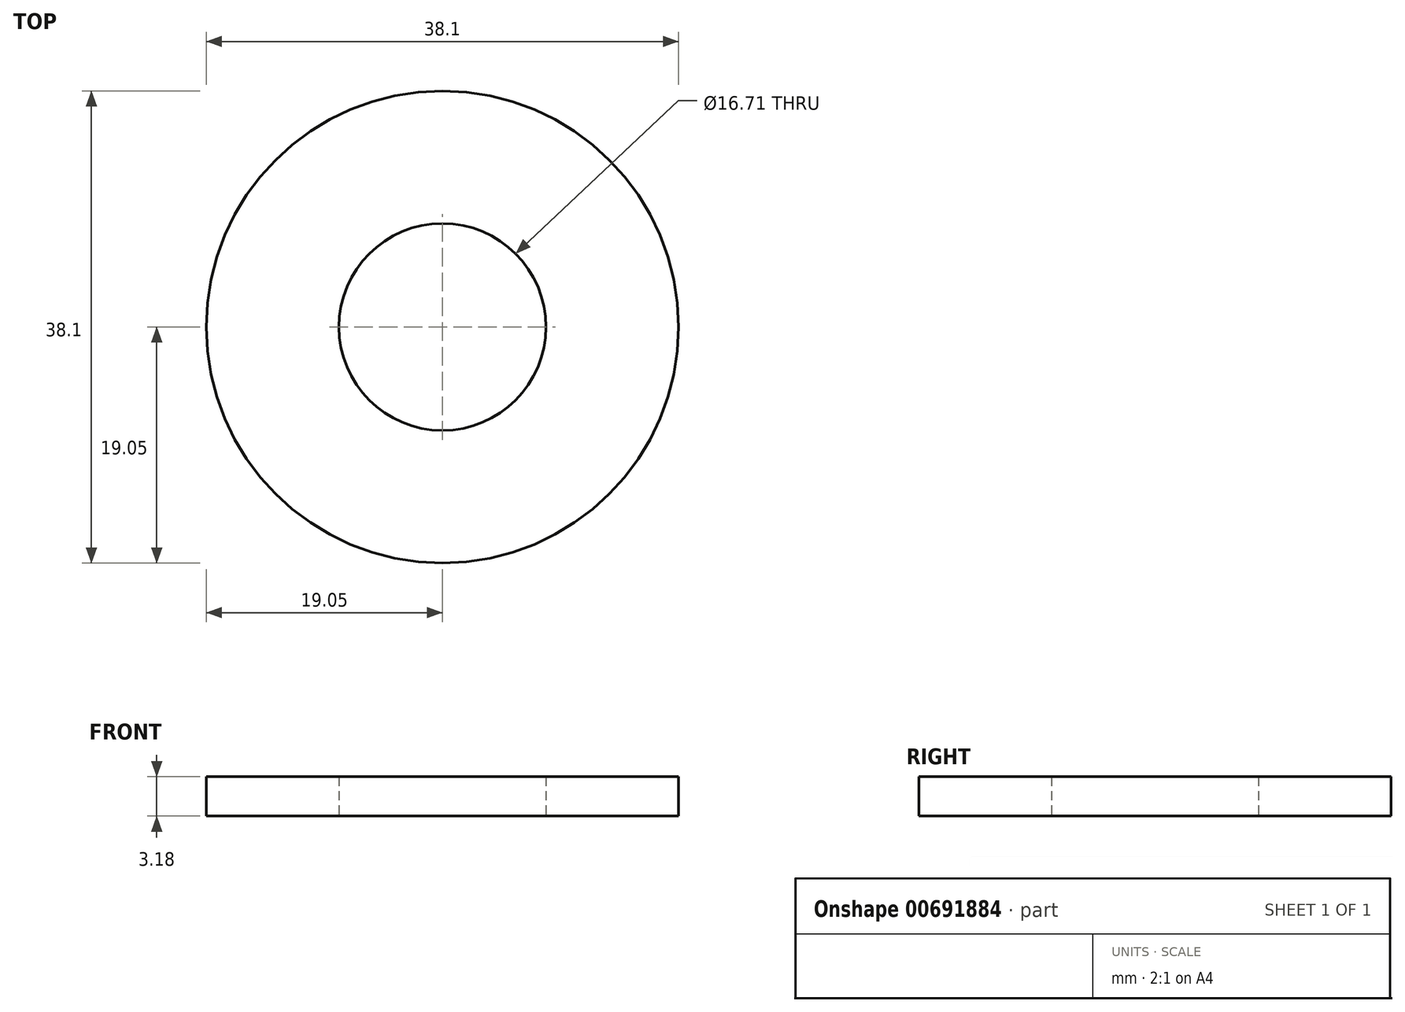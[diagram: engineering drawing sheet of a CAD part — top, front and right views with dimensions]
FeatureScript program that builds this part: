
annotation { "Feature Type Name" : "Feature", "Feature Type Description" : "" }
export const myFeature = defineFeature(function(context is Context, id is Id, definition is map)
    precondition{}
    {
        {
            var Q0;
            Q0=qCreatedBy(makeId("Top.planeOp"),FACE);
            var sketch = newSketch(context, id + "F0", { "sketchPlane" : qUnion([Q0])});
            skCircle(sketch, "E0", {"center": v(0, 0) * mm, "radius": 8.36 * mm});
            skCircle(sketch, "E1", {"center": v(0, 0) * mm, "radius": 19.05 * mm});
            skSolve(sketch);
        }
        {
            var Q0;
            Q0=makeQuery(id+"F0.imprint","IMPRINT",FACE,{"disambiguationData":[TD([[makeQuery(id+"F0.imprint","IMPRINT",EDGE,{"derivedFrom":sQuery(id+"F0.wireOp",EDGE,"E0")}),-1.0]])]});
            extrude(context, id + "F1", {"entities" : qUnion([Q0]), "depth" : 3.17 * mm, "offsetDistance" : 25.4 * mm});
        }
    });
